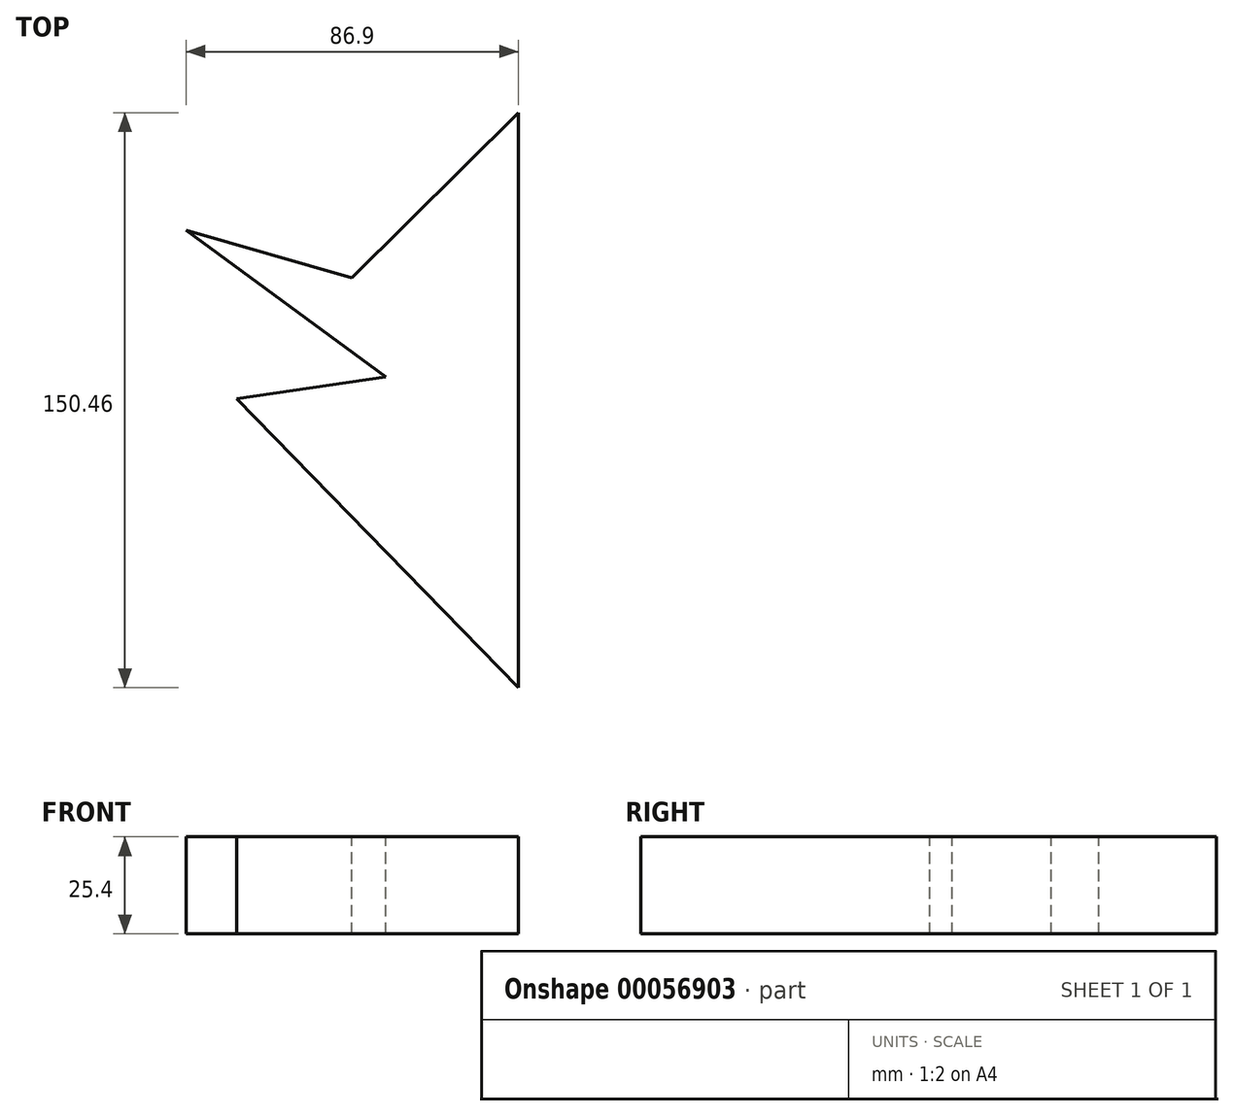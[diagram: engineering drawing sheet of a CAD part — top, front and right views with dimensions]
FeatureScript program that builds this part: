
annotation { "Feature Type Name" : "Feature", "Feature Type Description" : "" }
export const myFeature = defineFeature(function(context is Context, id is Id, definition is map)
    precondition{}
    {
        {
            var Q0;
            Q0=qCreatedBy(makeId("Top.planeOp"),FACE);
            var sketch = newSketch(context, id + "F0", { "sketchPlane" : qUnion([Q0])});
            skLineSegment(sketch, "E0", {"start": v(0, 0) * mm, "end": v(75.25, 74.46) * mm});
            skLineSegment(sketch, "E1", {"start": v(75.25, 74.46) * mm, "end": v(75.25, -76) * mm});
            skLineSegment(sketch, "E2", {"start": v(75.25, -76) * mm, "end": v(1.53, -0.4) * mm});
            skLineSegment(sketch, "E3", {"start": v(1.53, -0.4) * mm, "end": v(40.54, 5.32) * mm});
            skLineSegment(sketch, "E4", {"start": v(40.54, 5.32) * mm, "end": v(-11.65, 43.67) * mm});
            skLineSegment(sketch, "E5", {"start": v(-11.65, 43.67) * mm, "end": v(54.93, 24.6) * mm});
            skLineSegment(sketch, "E6", {"start": v(54.93, 24.6) * mm, "end": v(40.54, 5.32) * mm});
            skSolve(sketch);
        }
        {
            var Q0;
            {var subQ0=sQuery(id+"F0.wireOp",EDGE,"E4");var subQ1=sQuery(id+"F0.wireOp",EDGE,"E0");var subQ2=makeQuery(id+"F0.imprint","INTERSECT",VERTEX,{"derivedFrom":[subQ1,subQ0]});Q0=makeQuery(id+"F0.imprint","IMPRINT",FACE,{"disambiguationData":[TD([[makeQuery(id+"F0.imprint","IMPRINT",EDGE,{"disambiguationData":[TD([[subQ2,-1.0]])],"derivedFrom":subQ1}),1.0]])]});}
            var Q1;
            {var subQ0=sQuery(id+"F0.wireOp",EDGE,"E1");Q1=makeQuery(id+"F0.imprint","IMPRINT",FACE,{"disambiguationData":[TD([[makeQuery(id+"F0.imprint","IMPRINT",EDGE,{"derivedFrom":subQ0}),-1.0]])]});}
            var Q2;
            {var subQ5=sQuery(id+"F0.wireOp",EDGE,"E6");Q2=makeQuery(id+"F0.imprint","IMPRINT",FACE,{"disambiguationData":[TD([[makeQuery(id+"F0.imprint","IMPRINT",EDGE,{"derivedFrom":subQ5}),-1.0]])]});}
            extrude(context, id + "F1", {"entities" : qUnion([Q0, Q1, Q2]), "oppositeDirection" : true, "depth" : 25.4 * mm});
        }
    });
